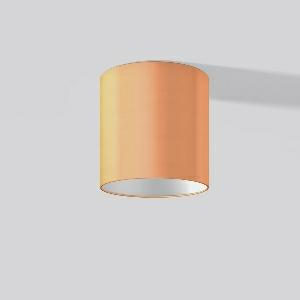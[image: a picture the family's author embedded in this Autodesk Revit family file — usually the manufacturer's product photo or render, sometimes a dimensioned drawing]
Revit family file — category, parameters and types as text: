
# Revit family: toledo_flatliner_901628_002_fee1
name_source: partatom
category: Lighting Fixtures
units: mm (PartAtom-declared; Revit-internal decimal feet)

## family parameters
Cut with Voids When Loaded = No
Host = Face
Light Source = No
Part Type = Normal
Room Calculation Point = No
Round Connector Dimension = Use Diameter
Shared = No

## types (1)
- 982299.002 (1 x LED Modul 830, 310 lm, 3000)
    Apparent Load = 5 VA
    CIE Flux Codes = 56 78 92 81 100
    Color Rendering = 80
    Color Temperature = 3000
    Default Elevation = 1800 mm
    Description = Series: TOLEDO FLATLINER
Decorative ceiling luminaire for interior decoration. Base luminaire prepared for the installation of fabric lampshade. Cylinder housing sheet steel, powder-coated. Housing: die cast aluminium and sheet steel, powder-coated. Bezel ring: die-cast aluminium, powder-coated. Lightguide and diffuser made of non-yellowing plastic (PMMA) opal matt. Modular design: With the basic luminaire, a square or cylindrical fabric lampshade must always be ordered separately. Fabric lampshades can be fitted to the basic luminaire without tools. Order satin finish diffuser as separate accessory. 
Colour: white
Diameter: 160 mm
Height: 65 mm
Lamp: LED
Socket: without socket
Colour temperature: 3000K
Colour rendering index (CRI): 80
System power: 5 W
Rated luminous flux: 310 lm
Luminous efficiency: 62 lm/W
Control gear: Regulated power supply
Protection class: II
Type of protection: IP 40
    Height = 65 mm
    Lamp = 1 x LED Modul 830
    Lamp Light Flux = 310 lm
    Lamp count = 1
    Length = 160 mm
    Lifetime = 50000 h
    Luminous efficacy = 62 lm/W
    Manufacturer = RZB
    ModVariant = No
    Model = 901628.002
    Mounting Place = Ceiling
    Mounting Type = Surface mounted
    Number of Poles = 1
    OnlyDefault = Yes
    Power Factor = 1
    Product Name = TOLEDO FLATLINER
    Product group = Surface mounted ceiling Fabric lampshade luminaires
    ProductGroupID = 313
    Protection Class = Protection class II
    Protection Degree = IP 40
    RLX_Detail_Level = 1
    RLX_Emergency_Light_Flux = 0 lm
    RLX_Emergency_Type = 0
    RLX_Emergency_Type_DB = No
    RlxData = <blob elided: 62285 chars, md5=0fdfd9cc>
    Socket = socket
    Standby Power = 0 W
    System Light Flux = 310 lm
    System Power = 5 W
    Type Image = toledo_flatliner_anbau_rund_orange_odeckel.jpg
    URL = http://relux.com
    VarID = 982299_002_f7b2
    Voltage = 230 V
    Voltage Range = 220-240 V
    Weight = 0.00 kg
    Width = 0 mm  [stored 0 ft]

note: [stored X ft] marks values corroborated as IEEE doubles in the binary element streams (Revit-internal decimal feet)

## geometry (parser evidence)
native form markers: Blend x4, Sweep x11
no freeform markers — native parametric forms only
